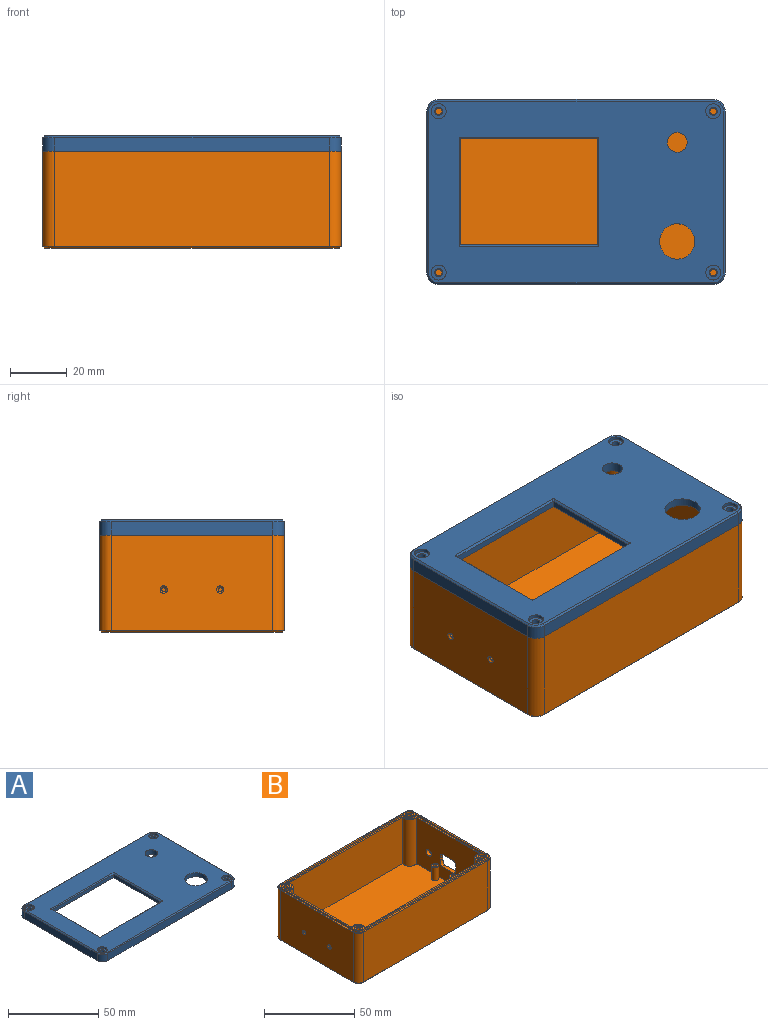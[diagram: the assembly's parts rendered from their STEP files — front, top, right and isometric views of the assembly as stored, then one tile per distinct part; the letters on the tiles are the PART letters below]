
ASSEMBLY  parts=2 mates=1
PART A: 97 faces, bbox 105.4x65.4x5.5 mm
  f0: cylinder r=1.3mm len=4.4mm, axis (0,0,1), area 35.9mm2, adj f68,f80
  f1: cylinder r=1.3mm len=4.4mm, axis (0,0,1), area 35.9mm2, adj f66,f79
  f2: cylinder r=1.3mm len=4.4mm, axis (0,0,1), area 35.9mm2, adj f64,f78
  f3: cylinder r=1.2mm len=4.4mm, axis (0,0,1), area 33.2mm2, adj f62,f77
  f4: cylinder r=1.4mm len=4.2mm, axis (0,0,1), area 36.9mm2, adj f28,f76
  f5: cylinder r=1.4mm len=4.2mm, axis (0,0,1), area 36.9mm2, adj f47,f74
  f6: cylinder r=1.4mm len=4.2mm, axis (0,0,1), area 36.9mm2, adj f49,f72
  f7: cylinder r=1.4mm len=4.2mm, axis (0,0,1), area 36.9mm2, adj f51,f70
  f8: plane 103.6x63.6mm, normal (0,0,-1), area 330.5mm2, adj f10,f11,f12,f13,f14,f15,f16,f17
  f9: plane 104.2x64.2mm, normal (0,0,1), area 4522.9mm2, adj f55,f59,f69,f71,f73,f75,f81,f82
  f10: plane 52.47x1mm, normal (1,0,0), area 52.5mm2, adj f8,f14,f15,f26
  f11: plane 92.47x1mm, normal (0,1,0), area 92.5mm2, adj f8,f15,f16,f26
  f12: plane 52.47x1mm, normal (-1,0,0), area 52.5mm2, adj f8,f16,f17,f26
  f13: plane 92.47x1mm, normal (0,-1,0), area 92.5mm2, adj f8,f14,f17,f26
  f14: cylinder r=3.3mm len=5.7mm, axis (0,0,1), area 10.6mm2, adj f8,f10,f13,f26
  f15: cylinder r=3.3mm len=5.7mm, axis (0,0,1), area 10.6mm2, adj f8,f10,f11,f26
  f16: cylinder r=3.3mm len=5.7mm, axis (0,0,1), area 10.6mm2, adj f8,f11,f12,f26
  f17: cylinder r=3.3mm len=5.7mm, axis (0,0,1), area 10.6mm2, adj f8,f12,f13,f26
  f18: plane 49.15x2.6mm, normal (-1,0,0), area 127.8mm2, adj f19,f25,f26,f57
  f19: cylinder r=4.2mm len=5.7mm, axis (0,0,1), area 25.1mm2, adj f18,f20,f26,f57
  f20: plane 89.15x2.6mm, normal (0,1,0), area 231.8mm2, adj f19,f21,f26,f57
  f21: cylinder r=4.2mm len=5.7mm, axis (0,0,1), area 25.1mm2, adj f20,f22,f26,f57
  f22: plane 49.15x2.6mm, normal (1,0,0), area 127.8mm2, adj f21,f23,f26,f57
  f23: cylinder r=4.2mm len=5.7mm, axis (0,0,1), area 25.1mm2, adj f22,f24,f26,f57
  f24: plane 89.15x2.6mm, normal (0,-1,0), area 231.8mm2, adj f23,f25,f26,f57
  f25: cylinder r=4.2mm len=5.7mm, axis (0,0,1), area 25.1mm2, adj f18,f24,f26,f57
  f26: plane 101.8x61.8mm, normal (0,0,-1), area 290.5mm2, adj f10,f11,f12,f13,f14,f15,f16,f17
  f27: cylinder r=2.4mm len=4.8mm, axis (0,0,1), area 15.1mm2, adj f8,f28
  f28: plane 4.8x4.8mm, normal (0,0,-1), area 11.9mm2, adj f4,f27
  f29: plane 57x1mm, normal (-1,0,0), area 57mm2, adj f8,f33,f34,f45
  f30: plane 97x1mm, normal (0,-1,0), area 97mm2, adj f8,f33,f36,f45
  f31: plane 57x1mm, normal (1,0,0), area 57mm2, adj f8,f35,f36,f45
  f32: plane 97x1mm, normal (0,1,0), area 97mm2, adj f8,f34,f35,f45
  f33: cylinder r=3.3mm len=3.3mm, axis (0,0,1), area 5.2mm2, adj f8,f29,f30,f45
  f34: cylinder r=3.3mm len=3.3mm, axis (0,0,1), area 5.2mm2, adj f8,f29,f32,f45
  f35: cylinder r=3.3mm len=3.3mm, axis (0,0,1), area 5.2mm2, adj f8,f31,f32,f45
  f36: cylinder r=3.3mm len=3.3mm, axis (0,0,1), area 5.2mm2, adj f8,f30,f31,f45
  f37: plane 57x4.8mm, normal (1,0,0), area 273.6mm2, adj f38,f44,f45,f81
  f38: cylinder r=4.2mm len=4.8mm, axis (0,0,1), area 31.7mm2, adj f37,f39,f45,f82
  f39: plane 97x4.8mm, normal (0,1,0), area 465.6mm2, adj f38,f40,f45,f84
  f40: cylinder r=4.2mm len=4.8mm, axis (0,0,1), area 31.7mm2, adj f39,f41,f45,f86
  f41: plane 57x4.8mm, normal (-1,0,0), area 273.6mm2, adj f40,f42,f45,f88
  f42: cylinder r=4.2mm len=4.8mm, axis (0,0,1), area 31.7mm2, adj f41,f43,f45,f87
  f43: plane 97x4.8mm, normal (0,-1,0), area 465.6mm2, adj f42,f44,f45,f85
  f44: cylinder r=4.2mm len=4.8mm, axis (0,0,1), area 31.7mm2, adj f37,f43,f45,f83
  f45: plane 105.4x65.4mm, normal (0,0,-1), area 298.4mm2, adj f29,f30,f31,f32,f33,f34,f35,f36
  f46: cylinder r=2.4mm len=4.8mm, axis (0,0,1), area 15.1mm2, adj f8,f47
  f47: plane 4.8x4.8mm, normal (0,0,-1), area 11.9mm2, adj f5,f46
  f48: cylinder r=2.4mm len=4.8mm, axis (0,0,1), area 15.1mm2, adj f8,f49
  f49: plane 4.8x4.8mm, normal (0,0,-1), area 11.9mm2, adj f6,f48
  f50: cylinder r=2.4mm len=4.8mm, axis (0,0,1), area 15.1mm2, adj f8,f51
  f51: plane 4.8x4.8mm, normal (0,0,-1), area 11.9mm2, adj f7,f50
  f52: plane 48.1x2.31mm, normal (0,-1,0), area 105.9mm2, adj f53,f56,f57,f90,f93,f95
  f53: plane 37.5x2.31mm, normal (-1,0,0), area 82.5mm2, adj f52,f54,f57,f89,f93,f94
  f54: plane 48.1x2.31mm, normal (0,1,0), area 105.9mm2, adj f53,f56,f57,f91,f94,f96
  f55: cylinder r=6.25mm len=12.5mm, axis (0,0,1), area 110mm2, adj f9,f57
  f56: plane 37.5x2.31mm, normal (1,0,0), area 82.5mm2, adj f52,f54,f57,f92,f95,f96
  f57: plane 100x60mm, normal (0,0,-1), area 3775.4mm2, adj f18,f19,f20,f21,f22,f23,f24,f25
  f58: cylinder r=6.2mm len=12.4mm, axis (0,0,1), area 23.4mm2, adj f57,f60
  f59: cylinder r=3.5mm len=7mm, axis (0,0,1), area 74.8mm2, adj f9,f60
  f60: plane 12.4x12.4mm, normal (0,0,-1), area 82.3mm2, adj f58,f59
  f61: cylinder r=2.25mm len=4.5mm, axis (0,0,1), area 36.8mm2, adj f57,f62
  f62: plane 4.5x4.5mm, normal (0,0,-1), area 11.4mm2, adj f3,f61
  f63: cylinder r=2.25mm len=4.5mm, axis (0,0,1), area 36.8mm2, adj f57,f64
  f64: plane 4.5x4.5mm, normal (0,0,-1), area 10.6mm2, adj f2,f63
  f65: cylinder r=2.25mm len=4.5mm, axis (0,0,1), area 36.8mm2, adj f57,f66
  f66: plane 4.5x4.5mm, normal (0,0,-1), area 10.6mm2, adj f1,f65
  f67: cylinder r=2.25mm len=4.5mm, axis (0,0,1), area 36.8mm2, adj f57,f68
  f68: plane 4.5x4.5mm, normal (0,0,-1), area 10.6mm2, adj f0,f67
  f69: cylinder r=2.62mm len=5.25mm, axis (0,0,1), area 19.8mm2, adj f9,f70
  f70: plane 5.25x5.25mm, normal (0,0,1), area 15.5mm2, adj f7,f69
  f71: cylinder r=2.62mm len=5.25mm, axis (0,0,1), area 19.8mm2, adj f9,f72
  f72: plane 5.25x5.25mm, normal (0,0,1), area 15.5mm2, adj f6,f71
  f73: cylinder r=2.62mm len=5.25mm, axis (0,0,1), area 19.8mm2, adj f9,f74
  f74: plane 5.25x5.25mm, normal (0,0,1), area 15.5mm2, adj f5,f73
  f75: cylinder r=2.62mm len=5.25mm, axis (0,0,1), area 19.8mm2, adj f9,f76
  f76: plane 5.25x5.25mm, normal (0,0,1), area 15.5mm2, adj f4,f75
  f77: plane 2.4x2.4mm, normal (0,0,-1), area 4.5mm2, adj f3
  f78: plane 2.6x2.6mm, normal (0,0,-1), area 5.3mm2, adj f2
  f79: plane 2.6x2.6mm, normal (0,0,-1), area 5.3mm2, adj f1
  f80: plane 2.6x2.6mm, normal (0,0,-1), area 5.3mm2, adj f0
  f81: plane 57x0.6mm, normal (0.71,0,0.71), area 48.4mm2, adj f9,f37,f82,f83
  f82: cone r=3.6mm half-angle=45deg, axis (0,0,-1), area 5.2mm2, adj f9,f38,f81,f84
  f83: cone r=3.6mm half-angle=45deg, axis (0,0,-1), area 5.2mm2, adj f9,f44,f81,f85
  f84: plane 97x0.6mm, normal (0,0.71,0.71), area 82.3mm2, adj f9,f39,f82,f86
  f85: plane 97x0.6mm, normal (0,-0.71,0.71), area 82.3mm2, adj f9,f43,f83,f87
  f86: cone r=3.6mm half-angle=45deg, axis (0,0,-1), area 5.2mm2, adj f9,f40,f84,f88
  f87: cone r=3.6mm half-angle=45deg, axis (0,0,-1), area 5.2mm2, adj f9,f42,f85,f88
  f88: plane 57x0.6mm, normal (-0.71,0,0.71), area 48.4mm2, adj f9,f41,f86,f87
  f89: plane 37.85x0.6mm, normal (-0.71,0,0.71), area 31.6mm2, adj f9,f53,f93,f94
  f90: plane 48.45x0.6mm, normal (0,-0.71,0.71), area 40.6mm2, adj f9,f52,f93,f95
  f91: plane 48.45x0.6mm, normal (0,0.71,0.71), area 40.6mm2, adj f9,f54,f94,f96
  f92: plane 37.85x0.6mm, normal (0.71,0,0.71), area 31.6mm2, adj f9,f56,f95,f96
  f93: cylinder r=0.6mm len=1.09mm, axis (-0.58,-0.58,-0.58), area 0.6mm2, adj f9,f52,f53,f89,f90
  f94: cylinder r=0.6mm len=1.09mm, axis (-0.58,0.58,-0.58), area 0.6mm2, adj f9,f53,f54,f89,f91
  f95: cylinder r=0.6mm len=1.09mm, axis (0.58,-0.58,-0.58), area 0.6mm2, adj f9,f52,f56,f90,f92
  f96: cylinder r=0.6mm len=1.09mm, axis (0.58,0.58,-0.58), area 0.6mm2, adj f9,f54,f56,f91,f92
PART B: 95 faces, bbox 105.5x65.5x35.3 mm
  f0: plane 49.15x31.4mm, normal (-1,0,0), area 1420.6mm2, adj f24,f30,f31,f48,f53,f54,f55,f56
  f1: plane 57.06x33.66mm, normal (1,0,0), area 1751.5mm2, adj f34,f40,f41,f66,f77,f78,f79,f80
  f2: plane 52.47x1mm, normal (-1,0,0), area 52.5mm2, adj f3,f21,f22,f31
  f3: cylinder r=3.3mm len=5.7mm, axis (0,0,-1), area 10.6mm2, adj f2,f4,f22,f31
  f4: plane 92.47x1mm, normal (0,1,0), area 92.5mm2, adj f3,f5,f22,f31
  f5: cylinder r=3.3mm len=5.7mm, axis (0,0,-1), area 10.6mm2, adj f4,f6,f22,f31
  f6: plane 52.47x1mm, normal (1,0,0), area 52.5mm2, adj f5,f7,f22,f31
  f7: cylinder r=3.3mm len=5.7mm, axis (0,0,-1), area 10.6mm2, adj f6,f8,f22,f31
  f8: plane 92.47x1mm, normal (0,-1,0), area 92.5mm2, adj f7,f21,f22,f31
  f9: plane 57x1mm, normal (1,0,0), area 57mm2, adj f10,f16,f22,f41
  f10: cylinder r=3.3mm len=3.3mm, axis (0,0,-1), area 5.2mm2, adj f9,f11,f22,f41
  f11: plane 97x1mm, normal (0,1,0), area 97mm2, adj f10,f12,f22,f41
  f12: cylinder r=3.3mm len=3.3mm, axis (0,0,-1), area 5.2mm2, adj f11,f13,f22,f41
  f13: plane 57x1mm, normal (-1,0,0), area 57mm2, adj f12,f14,f22,f41
  f14: cylinder r=3.3mm len=3.3mm, axis (0,0,-1), area 5.2mm2, adj f13,f15,f22,f41
  f15: plane 97x1mm, normal (0,-1,0), area 97mm2, adj f14,f16,f22,f41
  f16: cylinder r=3.3mm len=3.3mm, axis (0,0,-1), area 5.2mm2, adj f9,f15,f22,f41
  f17: cylinder r=2.4mm len=4.8mm, axis (0,0,-1), area 15.1mm2, adj f22,f33
  f18: cylinder r=2.4mm len=4.8mm, axis (0,0,-1), area 15.1mm2, adj f22,f43
  f19: cylinder r=2.4mm len=4.8mm, axis (0,0,-1), area 15.1mm2, adj f22,f45
  f20: cylinder r=2.4mm len=4.8mm, axis (0,0,-1), area 15.1mm2, adj f22,f47
  f21: cylinder r=3.3mm len=5.7mm, axis (0,0,-1), area 10.6mm2, adj f2,f8,f22,f31
  f22: plane 103.6x63.6mm, normal (0,0,1), area 330.5mm2, adj f2,f3,f4,f5,f6,f7,f8,f9
  f23: plane 104.2x64.2mm, normal (0,0,-1), area 6678.5mm2, adj f65,f66,f67,f68,f69,f70,f71,f72
  f24: cylinder r=4.2mm len=31.4mm, axis (0,0,-1), area 303.5mm2, adj f0,f25,f31,f48
  f25: plane 89.15x31.4mm, normal (0,1,0), area 2799.4mm2, adj f24,f26,f31,f48
  f26: cylinder r=4.2mm len=31.4mm, axis (0,0,-1), area 303.5mm2, adj f25,f27,f31,f48
  f27: plane 49.15x31.4mm, normal (1,0,0), area 1532.8mm2, adj f26,f28,f31,f48,f75,f76
  f28: cylinder r=4.2mm len=31.4mm, axis (0,0,-1), area 303.5mm2, adj f27,f29,f31,f48
  f29: plane 89.15x31.4mm, normal (0,-1,0), area 2799.4mm2, adj f28,f30,f31,f48
  f30: cylinder r=4.2mm len=31.4mm, axis (0,0,-1), area 303.5mm2, adj f0,f29,f31,f48
  f31: plane 101.8x61.8mm, normal (0,0,1), area 290.5mm2, adj f0,f2,f3,f4,f5,f6,f7,f8
  f32: cylinder r=1.2mm len=31.4mm, axis (0,0,-1), area 236.8mm2, adj f33,f49
  f33: plane 4.8x4.8mm, normal (0,0,1), area 13.6mm2, adj f17,f32
  f34: cylinder r=4.2mm len=33.6mm, axis (0,0,-1), area 221.7mm2, adj f1,f35,f41,f68
  f35: plane 97x33.6mm, normal (0,1,0), area 3259.2mm2, adj f34,f36,f41,f70
  f36: cylinder r=4.2mm len=33.6mm, axis (0,0,-1), area 221.7mm2, adj f35,f37,f41,f72
  f37: plane 57x33.6mm, normal (-1,0,0), area 1904.6mm2, adj f36,f38,f41,f71,f73,f74
  f38: cylinder r=4.2mm len=33.6mm, axis (0,0,-1), area 221.7mm2, adj f37,f39,f41,f69
  f39: plane 97x33.6mm, normal (0,-1,0), area 3259.2mm2, adj f38,f40,f41,f67
  f40: cylinder r=4.2mm len=33.6mm, axis (0,0,-1), area 221.7mm2, adj f1,f39,f41,f65
  f41: plane 105.4x65.4mm, normal (0,0,1), area 298.4mm2, adj f1,f9,f10,f11,f12,f13,f14,f15
  f42: cylinder r=1.2mm len=31.4mm, axis (0,0,-1), area 236.8mm2, adj f43,f50
  f43: plane 4.8x4.8mm, normal (0,0,1), area 13.6mm2, adj f18,f42
  f44: cylinder r=1.2mm len=31.4mm, axis (0,0,-1), area 236.8mm2, adj f45,f51
  f45: plane 4.8x4.8mm, normal (0,0,1), area 13.6mm2, adj f19,f44
  f46: cylinder r=1.2mm len=31.4mm, axis (0,0,-1), area 236.8mm2, adj f47,f52
  f47: plane 4.8x4.8mm, normal (0,0,1), area 13.6mm2, adj f20,f46
  f48: plane 100x60mm, normal (0,0,1), area 5863.6mm2, adj f0,f24,f25,f26,f27,f28,f29,f30
  f49: plane 2.4x2.4mm, normal (0,0,1), area 4.5mm2, adj f32
  f50: plane 2.4x2.4mm, normal (0,0,1), area 4.5mm2, adj f42
  f51: plane 2.4x2.4mm, normal (0,0,1), area 4.5mm2, adj f44
  f52: plane 2.4x2.4mm, normal (0,0,1), area 4.5mm2, adj f46
  f53: plane 2.1x2mm, normal (0,1,0), area 4.2mm2, adj f0,f54,f60,f78
  f54: extruded ~3.2x2.1mm, area 8.2mm2, adj f0,f53,f55,f77
  f55: plane 8.85x2.1mm, normal (0,0,-1), area 18.6mm2, adj f0,f54,f56,f79
  f56: extruded ~3.2x2.1mm, area 8.2mm2, adj f0,f55,f57,f81
  f57: plane 2.1x2mm, normal (0,-1,0), area 4.2mm2, adj f0,f56,f58,f83
  f58: extruded ~3.2x2.1mm, area 8.2mm2, adj f0,f57,f59,f84
  f59: plane 8.85x2.1mm, normal (0,0,1), area 18.6mm2, adj f0,f58,f60,f82
  f60: extruded ~3.2x2.1mm, area 8.2mm2, adj f0,f53,f59,f80
  f61: cylinder r=2mm len=4mm, axis (-1,0,0), area 26.4mm2, adj f0,f86
  f62: cylinder r=2mm len=4mm, axis (-1,0,0), area 26.4mm2, adj f0,f85
  f63: cylinder r=0.7mm len=1.5mm, axis (1,0,0), area 6.6mm2, adj f74,f75
  f64: cylinder r=0.7mm len=1.5mm, axis (1,0,0), area 6.6mm2, adj f73,f76
  f65: cone r=4.2mm half-angle=45deg, axis (0,0,1), area 5.2mm2, adj f23,f40,f66,f67
  f66: plane 57x0.6mm, normal (0.71,0,-0.71), area 48.4mm2, adj f1,f23,f65,f68
  f67: plane 97x0.6mm, normal (0,-0.71,-0.71), area 82.3mm2, adj f23,f39,f65,f69
  f68: cone r=4.2mm half-angle=45deg, axis (0,0,1), area 5.2mm2, adj f23,f34,f66,f70
  f69: cone r=4.2mm half-angle=45deg, axis (0,0,1), area 5.2mm2, adj f23,f38,f67,f71
  f70: plane 97x0.6mm, normal (0,0.71,-0.71), area 82.3mm2, adj f23,f35,f68,f72
  f71: plane 57x0.6mm, normal (-0.71,0,-0.71), area 48.4mm2, adj f23,f37,f69,f72
  f72: cone r=4.2mm half-angle=45deg, axis (0,0,1), area 5.2mm2, adj f23,f36,f70,f71
  f73: cone r=1.3mm half-angle=45deg, axis (-1,0,0), area 5.3mm2, adj f37,f64
  f74: cone r=1.3mm half-angle=45deg, axis (-1,0,0), area 5.3mm2, adj f37,f63
  f75: cone r=0.7mm half-angle=45deg, axis (1,0,0), area 5.3mm2, adj f27,f63
  f76: cone r=0.7mm half-angle=45deg, axis (1,0,0), area 5.3mm2, adj f27,f64
  f77: bspline ~3.8x2.28mm, area 3.7mm2, adj f1,f54,f78,f79
  f78: plane 2x0.6mm, normal (0.71,0.71,0), area 1.7mm2, adj f1,f53,f77,f80
  f79: plane 8.85x0.6mm, normal (0.71,0,-0.71), area 7.5mm2, adj f1,f55,f77,f81
  f80: bspline ~3.8x2.28mm, area 3.7mm2, adj f1,f60,f78,f82
  f81: bspline ~3.8x2.28mm, area 3.7mm2, adj f1,f56,f79,f83
  f82: plane 8.85x0.6mm, normal (0.71,0,0.71), area 7.5mm2, adj f1,f59,f80,f84
  f83: plane 2x0.6mm, normal (0.71,-0.71,0), area 1.7mm2, adj f1,f57,f81,f84
  f84: bspline ~3.8x2.28mm, area 3.7mm2, adj f1,f58,f82,f83
  f85: cone r=2mm half-angle=45deg, axis (1,0,0), area 12.3mm2, adj f1,f62
  f86: cone r=2mm half-angle=45deg, axis (1,0,0), area 12.3mm2, adj f1,f61
  f87: cylinder r=1mm len=9mm, axis (0,0,-1), area 56.5mm2, adj f89,f90
  f88: cylinder r=1.9mm len=9mm, axis (0,0,-1), area 107.4mm2, adj f48,f89
  f89: plane 3.8x3.8mm, normal (0,0,1), area 8.2mm2, adj f87,f88
  f90: plane 2x2mm, normal (0,0,1), area 3.1mm2, adj f87
  f91: cylinder r=1mm len=9mm, axis (0,0,-1), area 56.5mm2, adj f93,f94
  f92: cylinder r=1.9mm len=9mm, axis (0,0,-1), area 107.4mm2, adj f48,f93
  f93: plane 3.8x3.8mm, normal (0,0,1), area 8.2mm2, adj f91,f92
  f94: plane 2x2mm, normal (0,0,1), area 3.1mm2, adj f91
PLACE A at identity
PLACE B t=(0,-80,-39.6)mm
MATE fastened B.f3 <-> A.f6  axis (0,0,1) through (48.5,-28.5,-5.4)mm
